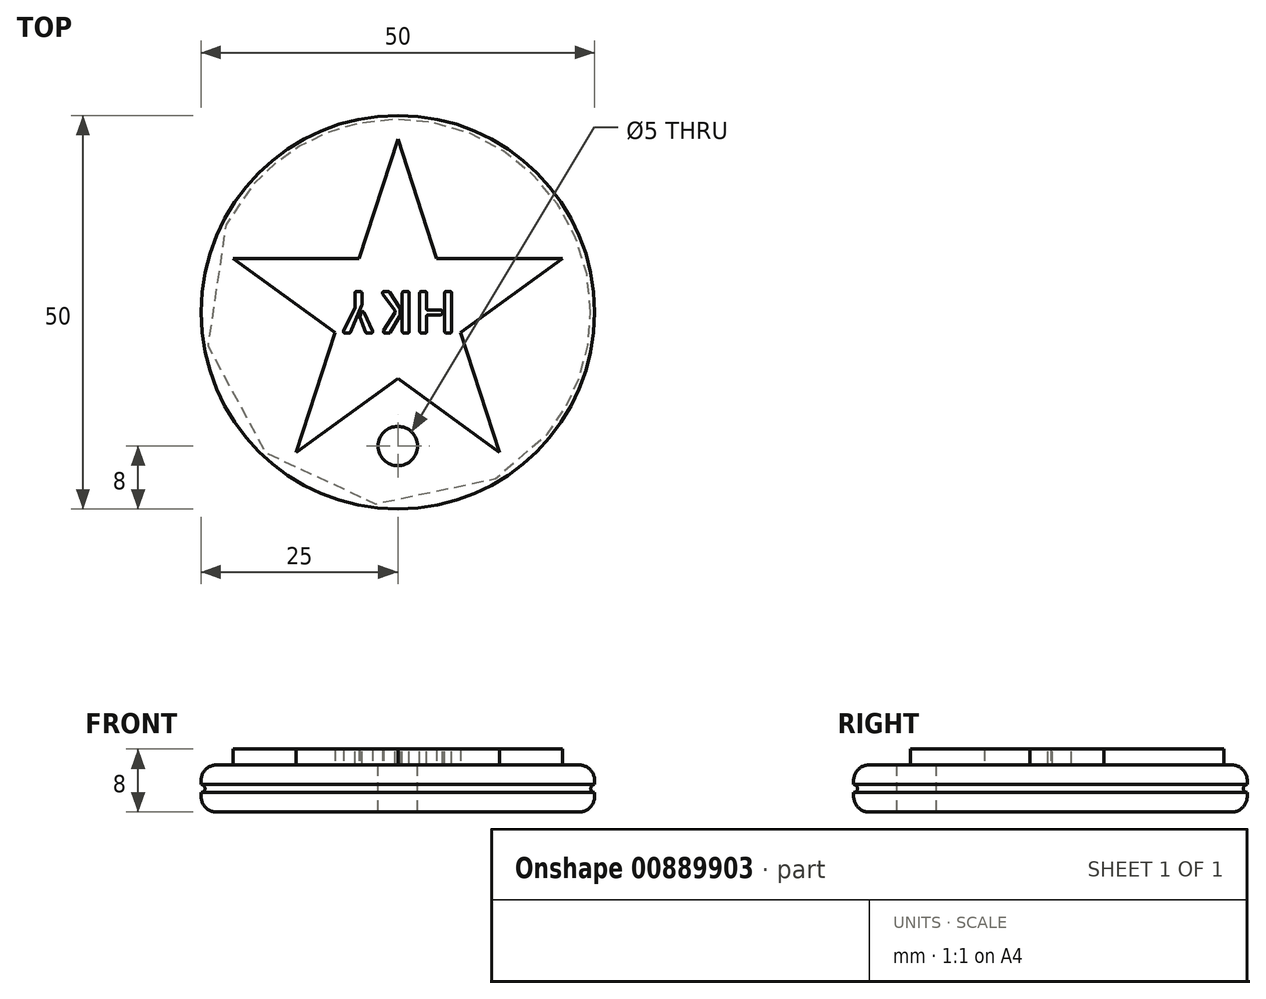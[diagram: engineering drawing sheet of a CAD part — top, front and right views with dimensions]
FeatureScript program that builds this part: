
annotation { "Feature Type Name" : "Feature", "Feature Type Description" : "" }
export const myFeature = defineFeature(function(context is Context, id is Id, definition is map)
    precondition{}
    {
        {
            var Q0;
            Q0=qCreatedBy(makeId("Top.planeOp"),FACE);
            var sketch = newSketch(context, id + "F0", { "sketchPlane" : qUnion([Q0])});
            skCircle(sketch, "E0", {"center": v(0, 0) * mm, "radius": 25 * mm});
            skSolve(sketch);
        }
        {
            var Q0;
            Q0=makeQuery(id+"F0.imprint","IMPRINT",FACE,{"disambiguationData":[TD([[makeQuery(id+"F0.imprint","IMPRINT",EDGE,{"derivedFrom":sQuery(id+"F0.wireOp",EDGE,"E0")}),1.0]])]});
            extrude(context, id + "F1", {"entities" : qUnion([Q0]), "depth" : 3 * mm, "offsetDistance" : 25 * mm, "hasSecondDirection" : true, "secondDirectionOppositeDirection" : true, "secondDirectionDepth" : 3 * mm});
        }
        {
            var Q0;
            Q0=makeQuery(id+"F1.opExtrude","CAP_EDGE",EDGE,{"disambiguationData":[OSD([sQuery(id+"F0.wireOp",EDGE,"E0")])],"isStart":false});
            var Q1;
            Q1=makeQuery(id+"F1.opExtrude","CAP_EDGE",EDGE,{"disambiguationData":[OSD([sQuery(id+"F0.wireOp",EDGE,"E0")])],"isStart":true});
            fillet(context, id + "F2", {"entities" : qUnion([Q0, Q1]), "radius" : 2 * mm, "tangentPropagation" : true, "allowEdgeOverflow" : false});
        }
        {
            var Q0;
            Q0=qCreatedBy(makeId("Top.planeOp"),FACE);
            var sketch = newSketch(context, id + "F3", { "sketchPlane" : qUnion([Q0])});
            skCircle(sketch, "E1.cCircle", {"center": v(0, 0) * mm, "radius": 22 * mm, "construction": true});
            skLineSegment(sketch, "E1.0", {"start": v(0, 22) * mm, "end": v(20.92, 6.8) * mm, "construction": true});
            skLineSegment(sketch, "E1.1", {"start": v(20.92, 6.8) * mm, "end": v(12.93, -17.8) * mm, "construction": true});
            skLineSegment(sketch, "E1.2", {"start": v(12.93, -17.8) * mm, "end": v(-12.93, -17.8) * mm, "construction": true});
            skLineSegment(sketch, "E1.3", {"start": v(-12.93, -17.8) * mm, "end": v(-20.92, 6.8) * mm, "construction": true});
            skLineSegment(sketch, "E1.4", {"start": v(-20.92, 6.8) * mm, "end": v(0, 22) * mm, "construction": true});
            skLineSegment(sketch, "E2", {"start": v(0, 22) * mm, "end": v(-4.94, 6.8) * mm});
            skLineSegment(sketch, "E3", {"start": v(-12.93, -17.8) * mm, "end": v(0, -8.4) * mm});
            skLineSegment(sketch, "E4", {"start": v(20.92, 6.8) * mm, "end": v(4.94, 6.8) * mm});
            skLineSegment(sketch, "E5", {"start": v(-20.92, 6.8) * mm, "end": v(-8, -2.6) * mm});
            skLineSegment(sketch, "E6", {"start": v(12.93, -17.8) * mm, "end": v(8, -2.6) * mm});
            skLineSegment(sketch, "E7.trimOffspring", {"start": v(-4.94, 6.8) * mm, "end": v(-20.92, 6.8) * mm});
            skLineSegment(sketch, "E8.trimOffspring", {"start": v(-8, -2.6) * mm, "end": v(-12.93, -17.8) * mm});
            skLineSegment(sketch, "E9.trimOffspring", {"start": v(0, -8.4) * mm, "end": v(12.93, -17.8) * mm});
            skLineSegment(sketch, "E10.trimOffspring", {"start": v(8, -2.6) * mm, "end": v(20.92, 6.8) * mm});
            skLineSegment(sketch, "E11.trimOffspring", {"start": v(4.94, 6.8) * mm, "end": v(0, 22) * mm});
            skSolve(sketch);
        }
        {
            var Q0;
            Q0=makeQuery(id+"F3.imprint","IMPRINT",FACE,{"disambiguationData":[TD([[makeQuery(id+"F3.imprint","IMPRINT",EDGE,{"derivedFrom":sQuery(id+"F3.wireOp",EDGE,"E2")}),1.0]])]});
            extrude(context, id + "F4", {"entities" : qUnion([Q0]), "operationType" : NewBodyOperationType.ADD, "depth" : 5 * mm, "offsetDistance" : 25 * mm, "hasSecondDirection" : true, "secondDirectionOppositeDirection" : true, "secondDirectionDepth" : 5 * mm});
        }
        {
            var Q0;
            Q0=makeQuery(id+"F1.opExtrude","CAP_FACE",FACE,{"disambiguationData":[OSD([sQuery(id+"F0.wireOp",EDGE,"E0")])],"isStart":false});
            var sketch = newSketch(context, id + "F5", { "sketchPlane" : qUnion([Q0])});
            skCircle(sketch, "E12", {"center": v(0, -17) * mm, "radius": 2.5 * mm});
            skSolve(sketch);
        }
        {
            var Q0;
            Q0=makeQuery(id+"F5.imprint","IMPRINT",FACE,{"disambiguationData":[TD([[makeQuery(id+"F5.imprint","IMPRINT",EDGE,{"derivedFrom":sQuery(id+"F5.wireOp",EDGE,"E12")}),1.0]])]});
            extrude(context, id + "F6", {"entities" : qUnion([Q0]), "operationType" : NewBodyOperationType.REMOVE, "oppositeDirection" : true, "depth" : 25 * mm, "offsetDistance" : 25 * mm});
        }
        {
            var Q0;
            Q0=makeQuery(id+"F4.opExtrude","CAP_FACE",FACE,{"disambiguationData":[OSD([sQuery(id+"F3.wireOp",EDGE,"E2"),sQuery(id+"F3.wireOp",EDGE,"E3"),sQuery(id+"F3.wireOp",EDGE,"E4"),sQuery(id+"F3.wireOp",EDGE,"E5"),sQuery(id+"F3.wireOp",EDGE,"E6"),sQuery(id+"F3.wireOp",EDGE,"E7.trimOffspring"),sQuery(id+"F3.wireOp",EDGE,"E8.trimOffspring"),sQuery(id+"F3.wireOp",EDGE,"E9.trimOffspring"),sQuery(id+"F3.wireOp",EDGE,"E10.trimOffspring"),sQuery(id+"F3.wireOp",EDGE,"E11.trimOffspring")])],"isStart":false});
            var sketch = newSketch(context, id + "F7", { "sketchPlane" : qUnion([Q0])});
            skText(sketch, "E13", { "text": "HKY", "fontName": "AllertaStencil-Regular.ttf"});
            skPoint(sketch, "E14", {"position": v(7.5, 0) * mm});
            const initialGuessF7  = {"E13": [0.0075, 0.00265, -1, 0, 0.0053]};
            skSetInitialGuess(sketch, initialGuessF7);
            skSolve(sketch);
        }
        {
            var Q0;
            Q0 = qSketchRegion(id + "F7", true);
            extrude(context, id + "F8", {"entities" : qUnion([Q0]), "operationType" : NewBodyOperationType.REMOVE, "oppositeDirection" : true, "depth" : 2 * mm, "offsetDistance" : 25 * mm});
        }
        {
            var Q0;
            Q0=makeQuery(id+"F8.boolean.opBoolean","COPY",EDGE,{"derivedFrom":makeQuery(id+"F8.opExtrude","SWEPT_EDGE",EDGE,{"disambiguationData":[OSD([sQuery(id+"F7.wireOp",EDGE,"E13.sketch_text.stroke-8"),sQuery(id+"F7.wireOp",EDGE,"E13.sketch_text.stroke-11")])]})});
            var Q1;
            Q1=makeQuery(id+"F8.boolean.opBoolean","COPY",EDGE,{"derivedFrom":makeQuery(id+"F8.opExtrude","SWEPT_EDGE",EDGE,{"disambiguationData":[OSD([sQuery(id+"F7.wireOp",EDGE,"E13.sketch_text.stroke-8"),sQuery(id+"F7.wireOp",EDGE,"E13.sketch_text.stroke-9")])]})});
            var Q2;
            Q2=makeQuery(id+"F8.boolean.opBoolean","COPY",EDGE,{"derivedFrom":makeQuery(id+"F8.opExtrude","SWEPT_EDGE",EDGE,{"disambiguationData":[OSD([sQuery(id+"F7.wireOp",EDGE,"E13.sketch_text.stroke-10"),sQuery(id+"F7.wireOp",EDGE,"E13.sketch_text.stroke-11")])]})});
            var Q3;
            Q3=makeQuery(id+"F8.boolean.opBoolean","COPY",EDGE,{"derivedFrom":makeQuery(id+"F8.opExtrude","SWEPT_EDGE",EDGE,{"disambiguationData":[OSD([sQuery(id+"F7.wireOp",EDGE,"E13.sketch_text.stroke-9"),sQuery(id+"F7.wireOp",EDGE,"E13.sketch_text.stroke-10")])]})});
            var Q4;
            Q4=makeQuery(id+"F8.boolean.opBoolean","COPY",EDGE,{"derivedFrom":makeQuery(id+"F8.opExtrude","CAP_EDGE",EDGE,{"disambiguationData":[OSD([sQuery(id+"F7.wireOp",EDGE,"E13.sketch_text.stroke-10")])],"isStart":false})});
            var Q5;
            Q5=makeQuery(id+"F8.boolean.opBoolean","COPY",EDGE,{"derivedFrom":makeQuery(id+"F8.opExtrude","CAP_EDGE",EDGE,{"disambiguationData":[OSD([sQuery(id+"F7.wireOp",EDGE,"E13.sketch_text.stroke-11")])],"isStart":false})});
            var Q6;
            Q6=makeQuery(id+"F8.boolean.opBoolean","COPY",EDGE,{"derivedFrom":makeQuery(id+"F8.opExtrude","CAP_EDGE",EDGE,{"disambiguationData":[OSD([sQuery(id+"F7.wireOp",EDGE,"E13.sketch_text.stroke-8")])],"isStart":false})});
            var Q7;
            Q7=makeQuery(id+"F8.boolean.opBoolean","COPY",EDGE,{"derivedFrom":makeQuery(id+"F8.opExtrude","CAP_EDGE",EDGE,{"disambiguationData":[OSD([sQuery(id+"F7.wireOp",EDGE,"E13.sketch_text.stroke-9")])],"isStart":false})});
            var Q8;
            Q8=makeQuery(id+"F8.boolean.opBoolean","COPY",EDGE,{"derivedFrom":makeQuery(id+"F8.opExtrude","SWEPT_EDGE",EDGE,{"disambiguationData":[OSD([sQuery(id+"F7.wireOp",EDGE,"E13.sketch_text.stroke-4"),sQuery(id+"F7.wireOp",EDGE,"E13.sketch_text.stroke-5")])]})});
            var Q9;
            Q9=makeQuery(id+"F8.boolean.opBoolean","COPY",EDGE,{"derivedFrom":makeQuery(id+"F8.opExtrude","CAP_EDGE",EDGE,{"disambiguationData":[OSD([sQuery(id+"F7.wireOp",EDGE,"E13.sketch_text.stroke-5")])],"isStart":false})});
            var Q10;
            Q10=makeQuery(id+"F8.boolean.opBoolean","COPY",FACE,{"derivedFrom":makeQuery(id+"F8.opExtrude","CAP_FACE",FACE,{"disambiguationData":[OSD([sQuery(id+"F7.wireOp",EDGE,"E13.sketch_text.stroke-0"),sQuery(id+"F7.wireOp",EDGE,"E13.sketch_text.stroke-1"),sQuery(id+"F7.wireOp",EDGE,"E13.sketch_text.stroke-2"),sQuery(id+"F7.wireOp",EDGE,"E13.sketch_text.stroke-3"),sQuery(id+"F7.wireOp",EDGE,"E13.sketch_text.stroke-4"),sQuery(id+"F7.wireOp",EDGE,"E13.sketch_text.stroke-5"),sQuery(id+"F7.wireOp",EDGE,"E13.sketch_text.stroke-6"),sQuery(id+"F7.wireOp",EDGE,"E13.sketch_text.stroke-7")])],"isStart":false})});
            var Q11;
            Q11=makeQuery(id+"F8.boolean.opBoolean","COPY",EDGE,{"derivedFrom":makeQuery(id+"F8.opExtrude","SWEPT_EDGE",EDGE,{"disambiguationData":[OSD([sQuery(id+"F7.wireOp",EDGE,"E13.sketch_text.stroke-3"),sQuery(id+"F7.wireOp",EDGE,"E13.sketch_text.stroke-4")])]})});
            var Q12;
            Q12=makeQuery(id+"F8.boolean.opBoolean","COPY",EDGE,{"derivedFrom":makeQuery(id+"F8.opExtrude","SWEPT_EDGE",EDGE,{"disambiguationData":[OSD([sQuery(id+"F7.wireOp",EDGE,"E13.sketch_text.stroke-2"),sQuery(id+"F7.wireOp",EDGE,"E13.sketch_text.stroke-3")])]})});
            var Q13;
            Q13=makeQuery(id+"F8.boolean.opBoolean","COPY",EDGE,{"derivedFrom":makeQuery(id+"F8.opExtrude","SWEPT_EDGE",EDGE,{"disambiguationData":[OSD([sQuery(id+"F7.wireOp",EDGE,"E13.sketch_text.stroke-5"),sQuery(id+"F7.wireOp",EDGE,"E13.sketch_text.stroke-6")])]})});
            var Q14;
            Q14=makeQuery(id+"F8.boolean.opBoolean","COPY",EDGE,{"derivedFrom":makeQuery(id+"F8.opExtrude","SWEPT_EDGE",EDGE,{"disambiguationData":[OSD([sQuery(id+"F7.wireOp",EDGE,"E13.sketch_text.stroke-1"),sQuery(id+"F7.wireOp",EDGE,"E13.sketch_text.stroke-2")])]})});
            var Q15;
            Q15=makeQuery(id+"F8.boolean.opBoolean","COPY",EDGE,{"derivedFrom":makeQuery(id+"F8.opExtrude","SWEPT_EDGE",EDGE,{"disambiguationData":[OSD([sQuery(id+"F7.wireOp",EDGE,"E13.sketch_text.stroke-0"),sQuery(id+"F7.wireOp",EDGE,"E13.sketch_text.stroke-1")])]})});
            var Q16;
            Q16=makeQuery(id+"F8.boolean.opBoolean","COPY",EDGE,{"derivedFrom":makeQuery(id+"F8.opExtrude","SWEPT_EDGE",EDGE,{"disambiguationData":[OSD([sQuery(id+"F7.wireOp",EDGE,"E13.sketch_text.stroke-6"),sQuery(id+"F7.wireOp",EDGE,"E13.sketch_text.stroke-7")])]})});
            var Q17;
            Q17=makeQuery(id+"F8.boolean.opBoolean","COPY",EDGE,{"derivedFrom":makeQuery(id+"F8.opExtrude","SWEPT_EDGE",EDGE,{"disambiguationData":[OSD([sQuery(id+"F7.wireOp",EDGE,"E13.sketch_text.stroke-0"),sQuery(id+"F7.wireOp",EDGE,"E13.sketch_text.stroke-7")])]})});
            var Q18;
            Q18=makeQuery(id+"F8.boolean.opBoolean","COPY",FACE,{"derivedFrom":makeQuery(id+"F8.opExtrude","CAP_FACE",FACE,{"disambiguationData":[OSD([sQuery(id+"F7.wireOp",EDGE,"E13.sketch_text.stroke-12"),sQuery(id+"F7.wireOp",EDGE,"E13.sketch_text.stroke-13"),sQuery(id+"F7.wireOp",EDGE,"E13.sketch_text.stroke-14"),sQuery(id+"F7.wireOp",EDGE,"E13.sketch_text.stroke-15")])],"isStart":false})});
            var Q19;
            Q19=makeQuery(id+"F8.boolean.opBoolean","COPY",FACE,{"derivedFrom":makeQuery(id+"F8.opExtrude","CAP_FACE",FACE,{"disambiguationData":[OSD([sQuery(id+"F7.wireOp",EDGE,"E13.sketch_text.stroke-16"),sQuery(id+"F7.wireOp",EDGE,"E13.sketch_text.stroke-17"),sQuery(id+"F7.wireOp",EDGE,"E13.sketch_text.stroke-18"),sQuery(id+"F7.wireOp",EDGE,"E13.sketch_text.stroke-19"),sQuery(id+"F7.wireOp",EDGE,"E13.sketch_text.stroke-20"),sQuery(id+"F7.wireOp",EDGE,"E13.sketch_text.stroke-21"),sQuery(id+"F7.wireOp",EDGE,"E13.sketch_text.stroke-22")])],"isStart":false})});
            var Q20;
            Q20=makeQuery(id+"F8.boolean.opBoolean","COPY",EDGE,{"derivedFrom":makeQuery(id+"F8.opExtrude","SWEPT_EDGE",EDGE,{"disambiguationData":[OSD([sQuery(id+"F7.wireOp",EDGE,"E13.sketch_text.stroke-12"),sQuery(id+"F7.wireOp",EDGE,"E13.sketch_text.stroke-13")])]})});
            var Q21;
            Q21=makeQuery(id+"F8.boolean.opBoolean","COPY",EDGE,{"derivedFrom":makeQuery(id+"F8.opExtrude","SWEPT_EDGE",EDGE,{"disambiguationData":[OSD([sQuery(id+"F7.wireOp",EDGE,"E13.sketch_text.stroke-12"),sQuery(id+"F7.wireOp",EDGE,"E13.sketch_text.stroke-15")])]})});
            var Q22;
            Q22=makeQuery(id+"F8.boolean.opBoolean","COPY",EDGE,{"derivedFrom":makeQuery(id+"F8.opExtrude","SWEPT_EDGE",EDGE,{"disambiguationData":[OSD([sQuery(id+"F7.wireOp",EDGE,"E13.sketch_text.stroke-14"),sQuery(id+"F7.wireOp",EDGE,"E13.sketch_text.stroke-15")])]})});
            var Q23;
            Q23=makeQuery(id+"F8.boolean.opBoolean","COPY",EDGE,{"derivedFrom":makeQuery(id+"F8.opExtrude","SWEPT_EDGE",EDGE,{"disambiguationData":[OSD([sQuery(id+"F7.wireOp",EDGE,"E13.sketch_text.stroke-13"),sQuery(id+"F7.wireOp",EDGE,"E13.sketch_text.stroke-14")])]})});
            var Q24;
            Q24=makeQuery(id+"F8.boolean.opBoolean","COPY",EDGE,{"derivedFrom":makeQuery(id+"F8.opExtrude","SWEPT_EDGE",EDGE,{"disambiguationData":[OSD([sQuery(id+"F7.wireOp",EDGE,"E13.sketch_text.stroke-20"),sQuery(id+"F7.wireOp",EDGE,"E13.sketch_text.stroke-21")])]})});
            var Q25;
            Q25=makeQuery(id+"F8.boolean.opBoolean","COPY",EDGE,{"derivedFrom":makeQuery(id+"F8.opExtrude","SWEPT_EDGE",EDGE,{"disambiguationData":[OSD([sQuery(id+"F7.wireOp",EDGE,"E13.sketch_text.stroke-19"),sQuery(id+"F7.wireOp",EDGE,"E13.sketch_text.stroke-20")])]})});
            var Q26;
            Q26=makeQuery(id+"F8.boolean.opBoolean","COPY",EDGE,{"derivedFrom":makeQuery(id+"F8.opExtrude","SWEPT_EDGE",EDGE,{"disambiguationData":[OSD([sQuery(id+"F7.wireOp",EDGE,"E13.sketch_text.stroke-18"),sQuery(id+"F7.wireOp",EDGE,"E13.sketch_text.stroke-19")])]})});
            var Q27;
            Q27=makeQuery(id+"F8.boolean.opBoolean","COPY",EDGE,{"derivedFrom":makeQuery(id+"F8.opExtrude","SWEPT_EDGE",EDGE,{"disambiguationData":[OSD([sQuery(id+"F7.wireOp",EDGE,"E13.sketch_text.stroke-17"),sQuery(id+"F7.wireOp",EDGE,"E13.sketch_text.stroke-18")])]})});
            var Q28;
            Q28=makeQuery(id+"F8.boolean.opBoolean","COPY",EDGE,{"derivedFrom":makeQuery(id+"F8.opExtrude","SWEPT_EDGE",EDGE,{"disambiguationData":[OSD([sQuery(id+"F7.wireOp",EDGE,"E13.sketch_text.stroke-16"),sQuery(id+"F7.wireOp",EDGE,"E13.sketch_text.stroke-17")])]})});
            var Q29;
            Q29=makeQuery(id+"F8.boolean.opBoolean","COPY",EDGE,{"derivedFrom":makeQuery(id+"F8.opExtrude","SWEPT_EDGE",EDGE,{"disambiguationData":[OSD([sQuery(id+"F7.wireOp",EDGE,"E13.sketch_text.stroke-16"),sQuery(id+"F7.wireOp",EDGE,"E13.sketch_text.stroke-22")])]})});
            var Q30;
            Q30=makeQuery(id+"F8.boolean.opBoolean","COPY",EDGE,{"derivedFrom":makeQuery(id+"F8.opExtrude","SWEPT_EDGE",EDGE,{"disambiguationData":[OSD([sQuery(id+"F7.wireOp",EDGE,"E13.sketch_text.stroke-21"),sQuery(id+"F7.wireOp",EDGE,"E13.sketch_text.stroke-22")])]})});
            var Q31;
            Q31=makeQuery(id+"F8.boolean.opBoolean","COPY",EDGE,{"derivedFrom":makeQuery(id+"F8.opExtrude","SWEPT_EDGE",EDGE,{"disambiguationData":[OSD([sQuery(id+"F7.wireOp",EDGE,"E13.sketch_text.stroke-31"),sQuery(id+"F7.wireOp",EDGE,"E13.sketch_text.stroke-32")])]})});
            var Q32;
            Q32=makeQuery(id+"F8.boolean.opBoolean","COPY",EDGE,{"derivedFrom":makeQuery(id+"F8.opExtrude","CAP_EDGE",EDGE,{"disambiguationData":[OSD([sQuery(id+"F7.wireOp",EDGE,"E13.sketch_text.stroke-32")])],"isStart":false})});
            var Q33;
            Q33=makeQuery(id+"F8.boolean.opBoolean","COPY",FACE,{"derivedFrom":makeQuery(id+"F8.opExtrude","CAP_FACE",FACE,{"disambiguationData":[OSD([sQuery(id+"F7.wireOp",EDGE,"E13.sketch_text.stroke-29"),sQuery(id+"F7.wireOp",EDGE,"E13.sketch_text.stroke-30"),sQuery(id+"F7.wireOp",EDGE,"E13.sketch_text.stroke-31"),sQuery(id+"F7.wireOp",EDGE,"E13.sketch_text.stroke-32")])],"isStart":false})});
            var Q34;
            Q34=makeQuery(id+"F8.boolean.opBoolean","COPY",EDGE,{"derivedFrom":makeQuery(id+"F8.opExtrude","SWEPT_EDGE",EDGE,{"disambiguationData":[OSD([sQuery(id+"F7.wireOp",EDGE,"E13.sketch_text.stroke-29"),sQuery(id+"F7.wireOp",EDGE,"E13.sketch_text.stroke-32")])]})});
            var Q35;
            Q35=makeQuery(id+"F8.boolean.opBoolean","COPY",EDGE,{"derivedFrom":makeQuery(id+"F8.opExtrude","SWEPT_EDGE",EDGE,{"disambiguationData":[OSD([sQuery(id+"F7.wireOp",EDGE,"E13.sketch_text.stroke-29"),sQuery(id+"F7.wireOp",EDGE,"E13.sketch_text.stroke-30")])]})});
            var Q36;
            Q36=makeQuery(id+"F8.boolean.opBoolean","COPY",EDGE,{"derivedFrom":makeQuery(id+"F8.opExtrude","SWEPT_EDGE",EDGE,{"disambiguationData":[OSD([sQuery(id+"F7.wireOp",EDGE,"E13.sketch_text.stroke-30"),sQuery(id+"F7.wireOp",EDGE,"E13.sketch_text.stroke-31")])]})});
            var Q37;
            Q37=makeQuery(id+"F8.boolean.opBoolean","COPY",FACE,{"derivedFrom":makeQuery(id+"F8.opExtrude","CAP_FACE",FACE,{"disambiguationData":[OSD([sQuery(id+"F7.wireOp",EDGE,"E13.sketch_text.stroke-23"),sQuery(id+"F7.wireOp",EDGE,"E13.sketch_text.stroke-24"),sQuery(id+"F7.wireOp",EDGE,"E13.sketch_text.stroke-25"),sQuery(id+"F7.wireOp",EDGE,"E13.sketch_text.stroke-26"),sQuery(id+"F7.wireOp",EDGE,"E13.sketch_text.stroke-27"),sQuery(id+"F7.wireOp",EDGE,"E13.sketch_text.stroke-28")])],"isStart":false})});
            var Q38;
            Q38=makeQuery(id+"F8.boolean.opBoolean","COPY",EDGE,{"derivedFrom":makeQuery(id+"F8.opExtrude","SWEPT_EDGE",EDGE,{"disambiguationData":[OSD([sQuery(id+"F7.wireOp",EDGE,"E13.sketch_text.stroke-23"),sQuery(id+"F7.wireOp",EDGE,"E13.sketch_text.stroke-28")])]})});
            var Q39;
            Q39=makeQuery(id+"F8.boolean.opBoolean","COPY",EDGE,{"derivedFrom":makeQuery(id+"F8.opExtrude","SWEPT_EDGE",EDGE,{"disambiguationData":[OSD([sQuery(id+"F7.wireOp",EDGE,"E13.sketch_text.stroke-23"),sQuery(id+"F7.wireOp",EDGE,"E13.sketch_text.stroke-24")])]})});
            var Q40;
            Q40=makeQuery(id+"F8.boolean.opBoolean","COPY",EDGE,{"derivedFrom":makeQuery(id+"F8.opExtrude","SWEPT_EDGE",EDGE,{"disambiguationData":[OSD([sQuery(id+"F7.wireOp",EDGE,"E13.sketch_text.stroke-27"),sQuery(id+"F7.wireOp",EDGE,"E13.sketch_text.stroke-28")])]})});
            var Q41;
            Q41=makeQuery(id+"F8.boolean.opBoolean","COPY",EDGE,{"derivedFrom":makeQuery(id+"F8.opExtrude","SWEPT_EDGE",EDGE,{"disambiguationData":[OSD([sQuery(id+"F7.wireOp",EDGE,"E13.sketch_text.stroke-26"),sQuery(id+"F7.wireOp",EDGE,"E13.sketch_text.stroke-27")])]})});
            var Q42;
            Q42=makeQuery(id+"F8.boolean.opBoolean","COPY",EDGE,{"derivedFrom":makeQuery(id+"F8.opExtrude","SWEPT_EDGE",EDGE,{"disambiguationData":[OSD([sQuery(id+"F7.wireOp",EDGE,"E13.sketch_text.stroke-25"),sQuery(id+"F7.wireOp",EDGE,"E13.sketch_text.stroke-26")])]})});
            var Q43;
            Q43=makeQuery(id+"F8.boolean.opBoolean","COPY",EDGE,{"derivedFrom":makeQuery(id+"F8.opExtrude","SWEPT_EDGE",EDGE,{"disambiguationData":[OSD([sQuery(id+"F7.wireOp",EDGE,"E13.sketch_text.stroke-24"),sQuery(id+"F7.wireOp",EDGE,"E13.sketch_text.stroke-25")])]})});
            fillet(context, id + "F9", {"entities" : qUnion([Q0, Q1, Q2, Q3, Q4, Q5, Q6, Q7, Q8, Q9, Q10, Q11, Q12, Q13, Q14, Q15, Q16, Q17, Q18, Q19, Q20, Q21, Q22, Q23, Q24, Q25, Q26, Q27, Q28, Q29, Q30, Q31, Q32, Q33, Q34, Q35, Q36, Q37, Q38, Q39, Q40, Q41, Q42, Q43]), "radius" : 0.2 * mm, "tangentPropagation" : true, "allowEdgeOverflow" : false});
        }
        {
            var Q0;
            Q0=qCreatedBy(makeId("Top.planeOp"),FACE);
            var sketch = newSketch(context, id + "F10", { "sketchPlane" : qUnion([Q0])});
            skCircle(sketch, "E15", {"center": v(0, 0) * mm, "radius": 24.25 * mm});
            skSolve(sketch);
        }
        {
            var Q0;
            Q0=qCreatedBy(makeId("Front.planeOp"),FACE);
            var sketch = newSketch(context, id + "F11", { "sketchPlane" : qUnion([Q0])});
            skCircle(sketch, "E16", {"center": v(25, 0) * mm, "radius": 0.5 * mm});
            skSolve(sketch);
        }
        {
            var Q0;
            Q0=makeQuery(id+"F11.imprint","IMPRINT",FACE,{"disambiguationData":[TD([[makeQuery(id+"F11.imprint","IMPRINT",EDGE,{"derivedFrom":sQuery(id+"F11.wireOp",EDGE,"E16")}),1.0]])]});
            var Q1;
            Q1=sQuery(id+"F10.wireOp",EDGE,"E15");
            sweep(context, id + "F12", {"operationType" : NewBodyOperationType.REMOVE, "profiles" : qUnion([Q0]), "path" : qUnion([Q1])});
        }
        {
            var Q0;
            Q0=makeQuery(id+"F4.opExtrude","CAP_FACE",FACE,{"disambiguationData":[OSD([sQuery(id+"F3.wireOp",EDGE,"E2"),sQuery(id+"F3.wireOp",EDGE,"E3"),sQuery(id+"F3.wireOp",EDGE,"E4"),sQuery(id+"F3.wireOp",EDGE,"E5"),sQuery(id+"F3.wireOp",EDGE,"E6"),sQuery(id+"F3.wireOp",EDGE,"E7.trimOffspring"),sQuery(id+"F3.wireOp",EDGE,"E8.trimOffspring"),sQuery(id+"F3.wireOp",EDGE,"E9.trimOffspring"),sQuery(id+"F3.wireOp",EDGE,"E10.trimOffspring"),sQuery(id+"F3.wireOp",EDGE,"E11.trimOffspring")])],"isStart":true});
            var Q1;
            Q1=makeQuery(id+"F1.opExtrude","CAP_FACE",FACE,{"disambiguationData":[OSD([sQuery(id+"F0.wireOp",EDGE,"E0")])],"isStart":true});
            extrude(context, id + "F13", {"entities" : qUnion([Q0]), "operationType" : NewBodyOperationType.REMOVE, "endBound" : BoundingType.UP_TO_SURFACE, "oppositeDirection" : true, "depth" : 25 * mm, "endBoundEntityFace" : qUnion([Q1]), "offsetDistance" : 25 * mm});
        }
    });
